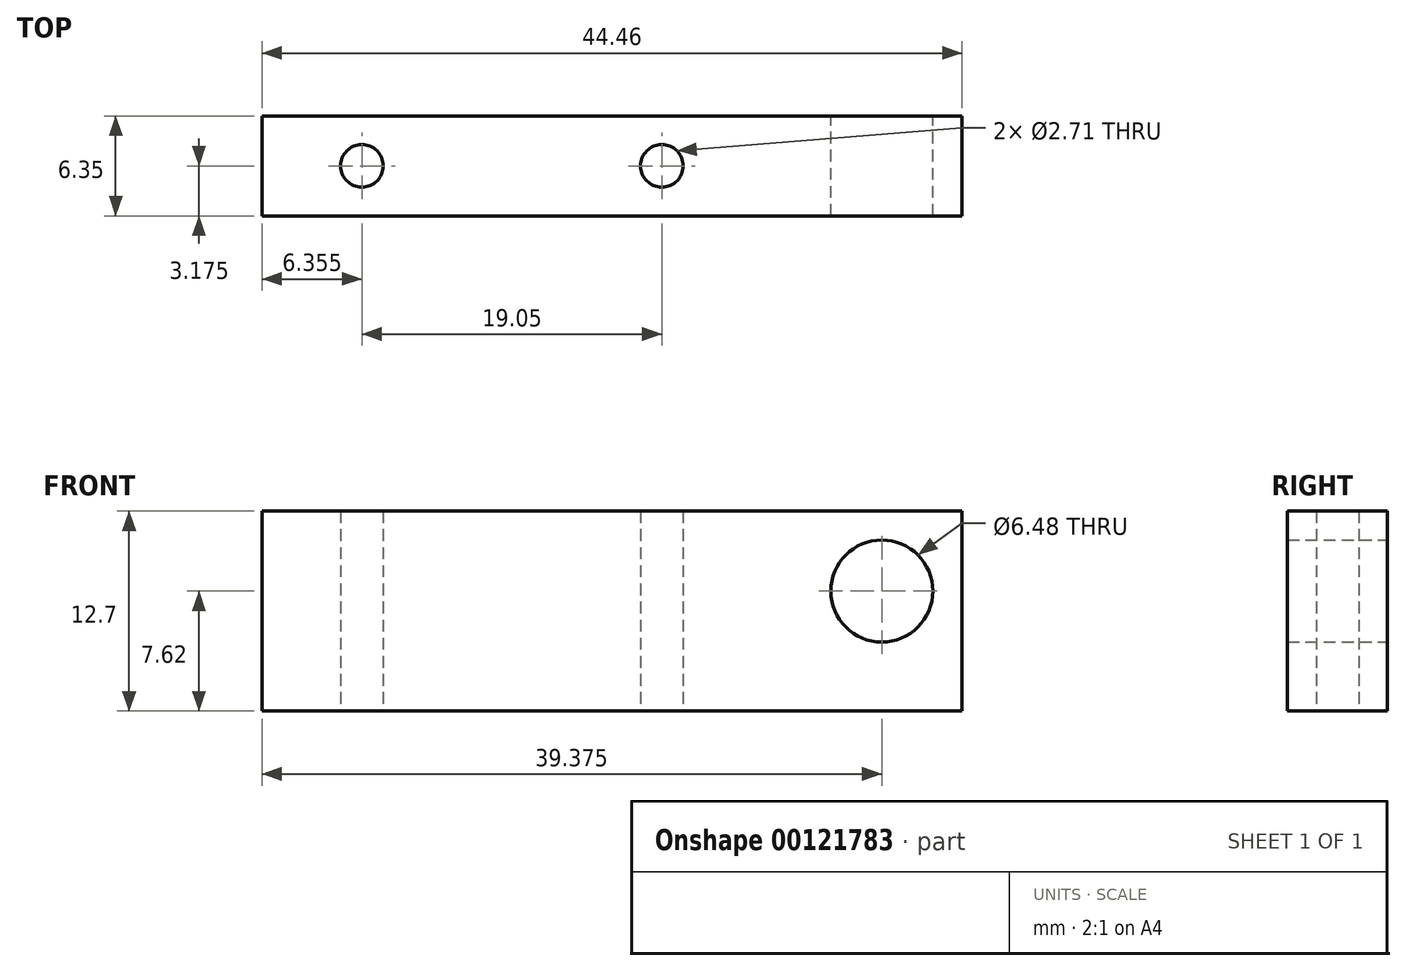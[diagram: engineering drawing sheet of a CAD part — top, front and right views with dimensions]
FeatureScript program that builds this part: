
annotation { "Feature Type Name" : "Feature", "Feature Type Description" : "" }
export const myFeature = defineFeature(function(context is Context, id is Id, definition is map)
    precondition{}
    {
        {
            var Q0;
            Q0=qCreatedBy(makeId("Front.planeOp"),FACE);
            var sketch = newSketch(context, id + "F0", { "sketchPlane" : qUnion([Q0])});
            skLineSegment(sketch, "E0.bottom", {"start": v(22.23, -6.35) * mm, "end": v(-22.23, -6.35) * mm});
            skLineSegment(sketch, "E0.top", {"start": v(22.22, 6.35) * mm, "end": v(-22.23, 6.35) * mm});
            skLineSegment(sketch, "E0.left", {"start": v(22.23, -6.35) * mm, "end": v(22.22, 6.35) * mm});
            skLineSegment(sketch, "E0.right", {"start": v(-22.23, -6.35) * mm, "end": v(-22.23, 6.35) * mm});
            skPoint(sketch, "E0.middle", {"position": v(0, 0) * mm});
            skCircle(sketch, "E1", {"center": v(17.14, 1.27) * mm, "radius": 3.24 * mm});
            skSolve(sketch);
        }
        {
            var Q0;
            Q0 = qSketchRegion(id + "F0", true);
            extrude(context, id + "F1", {"entities" : qUnion([Q0]), "depth" : 6.35 * mm});
        }
        {
            var Q0;
            Q0=makeQuery(id+"F1.opExtrude","SWEPT_FACE",FACE,{"disambiguationData":[OSD([sQuery(id+"F0.wireOp",EDGE,"E0.bottom")])]});
            var sketch = newSketch(context, id + "F2", { "sketchPlane" : qUnion([Q0])});
            skPoint(sketch, "E2", {"position": v(3.18, 3.18) * mm});
            skPoint(sketch, "E3", {"position": v(-15.88, 3.18) * mm});
            skSolve(sketch);
        }
        {
            var Q0;
            Q0=sQuery(id+"F2.wireOp",VERTEX,"E3");
            var Q1;
            Q1=sQuery(id+"F2.wireOp",VERTEX,"E2");
            var Q2;
            Q2=makeQuery(id+"F1.opExtrude","SWEPT_BODY",BODY,{"disambiguationData":[OSD([sQuery(id+"F0.wireOp",EDGE,"E0.bottom"),sQuery(id+"F0.wireOp",EDGE,"E0.top"),sQuery(id+"F0.wireOp",EDGE,"E0.left"),sQuery(id+"F0.wireOp",EDGE,"E0.right"),sQuery(id+"F0.wireOp",EDGE,"E1")])]});
            hole(context, id + "F3", {"style" : HoleStyle.SIMPLE, "endStyle" : HoleEndStyle.THROUGH, "standardTappedOrClearance" : lookupTablePath({ "standard" : "ANSI", "engagement" : "75%", "pitch" : "32 tpi", "size" : "#6", "type" : "Tapped" }), "standardBlindInLast" : lookupTablePath({ "standard" : "ANSI", "engagement" : "75%", "pitch" : "32 tpi", "size" : "#6", "type" : "Tapped" }), "holeDiameter" : 2.7 * mm, "locations" : qUnion([Q0, Q1]), "scope" : qUnion([Q2]), "isTappedThrough" : true, "majorDiameter" : 3.5 * mm, "showTappedDepth" : true});
        }
    });
